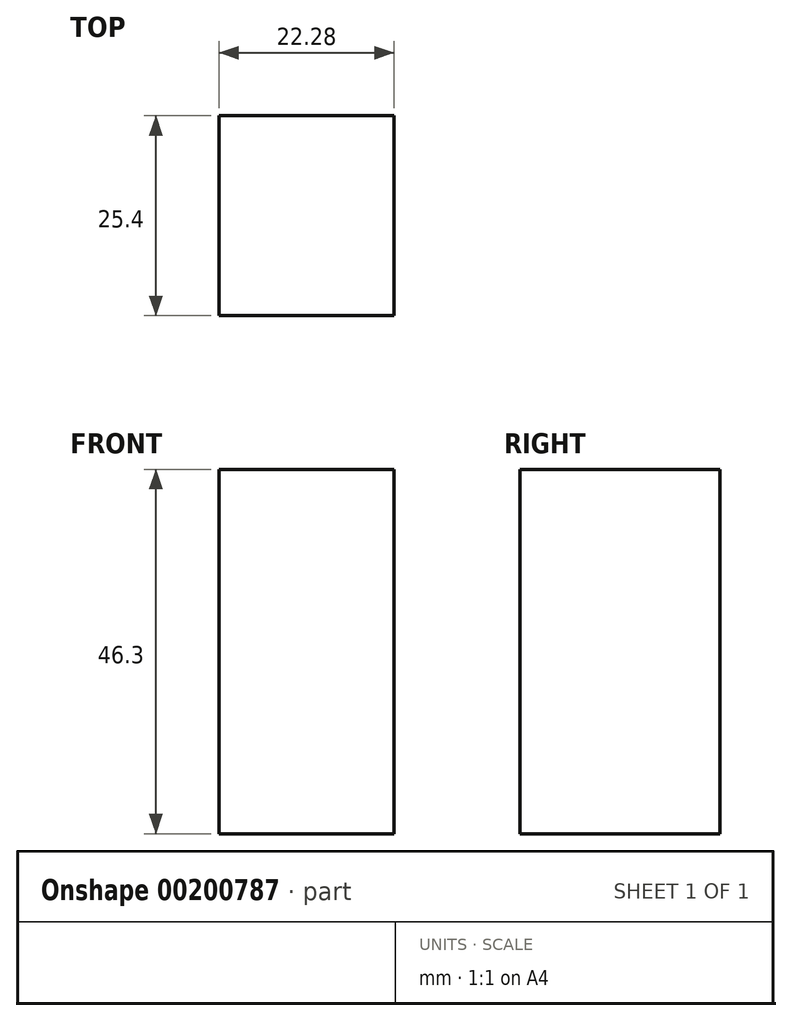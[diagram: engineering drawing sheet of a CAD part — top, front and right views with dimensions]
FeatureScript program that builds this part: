
annotation { "Feature Type Name" : "Feature", "Feature Type Description" : "" }
export const myFeature = defineFeature(function(context is Context, id is Id, definition is map)
    precondition{}
    {
        {
            var Q0;
            Q0=qCreatedBy(makeId("Front.planeOp"),FACE);
            var sketch = newSketch(context, id + "F0", { "sketchPlane" : qUnion([Q0])});
            skLineSegment(sketch, "E0", {"start": v(-30.38, 39.2) * mm, "end": v(-30.38, 7.38) * mm});
            skLineSegment(sketch, "E1", {"start": v(-30.38, 39.2) * mm, "end": v(-8.1, 39.2) * mm});
            skLineSegment(sketch, "E2", {"start": v(-8.1, 39.2) * mm, "end": v(-8.1, 7.38) * mm});
            skLineSegment(sketch, "E3", {"start": v(-30.38, 7.38) * mm, "end": v(-8.1, 7.38) * mm});
            skLineSegment(sketch, "E4", {"start": v(-30.38, 7.38) * mm, "end": v(-30.38, 0) * mm});
            skLineSegment(sketch, "E5", {"start": v(-30.38, 0) * mm, "end": v(-30.38, -7.09) * mm});
            skLineSegment(sketch, "E6", {"start": v(-30.38, -7.09) * mm, "end": v(-8.1, -7.09) * mm});
            skLineSegment(sketch, "E7", {"start": v(-8.1, -7.09) * mm, "end": v(-8.1, 0) * mm});
            skLineSegment(sketch, "E8", {"start": v(-8.1, 0) * mm, "end": v(-8.1, 7.38) * mm});
            skLineSegment(sketch, "E9", {"start": v(-30.38, 0) * mm, "end": v(-8.1, 0) * mm});
            skSolve(sketch);
        }
        {
            var Q0;
            Q0 = qSketchRegion(id + "F0", true);
            extrude(context, id + "F1", {"entities" : qUnion([Q0]), "depth" : 25.4 * mm});
        }
    });
